# Revit family: Sideboard-Teknion-CFBQL_Figure_36H_Quad_Sideboard_Low_Base-R2023
name_source: partatom
category: Furniture
units: mm (PartAtom-declared; Revit-internal decimal feet)

## family parameters
Always vertical = Yes
Cut with Voids When Loaded = No
Enable Cutting in Views = No
OmniClass Number = 23.40.20.00
OmniClass Title = General Furniture and Specialties
Render Appearance Source = Family Geometry
Room Calculation Point = No
Shared = Yes
Work Plane-Based = No

## types (5) — shared parameters
Assembly Code = E2020200
Description = 36H Quad Sideboard, Low Base
Glide Finish = Paint-Teknion-23-Z-Foundation-Foundry Onyx
Manufacturer = Teknion
Manufacturer Fax = 416.661.4586
Part Number = CFBQL
Product Documentation Link = https://d2r72yk5wmppdj.cloudfront.net
Product Line = Figure - Sideboards
Product Page URL = https://www.teknion.com
Series = Custom Wood
Sustainability Data = https://www.teknion.com
URL = www.teknion.com
Unit Weight URL = http://www.teknion.com
Warranty = http://www.teknion.com
zero-valued in all types: Default Elevation

## per-type parameters (varying)
| type | HCCH | HDDH | HHHH | HWCH | HWDH | Left Door Cutout | Model | Right Door Cutout |
| (HHHH) All H.Doors | No | No | Yes | No | No | Yes | CFBQL_HHHH_ | Yes |
| (HCCH) H.Door / x2 Cutouts for AV or Fridge / H.Door | Yes | No | No | No | No | Yes | CFBQL_HCCH_ | Yes |
| (HWCH) H.Door / Waste / Cutouts for AV or Fridge / H.Door | No | No | No | Yes | No | No | CFBQL_HWCH__ | Yes |
| (HWDH) H.Door / Waste / Casual Drawer / H.Door | No | No | No | No | Yes | No | CFBQL_HWDH_ | No |
| (HDDH) H.Door / x2 Casual Drawer / H.Door | No | Yes | No | No | No | No | CFBQL_HDDH_ | No |

## geometry (parser evidence)
native form markers: Sweep x7
no freeform markers — native parametric forms only
